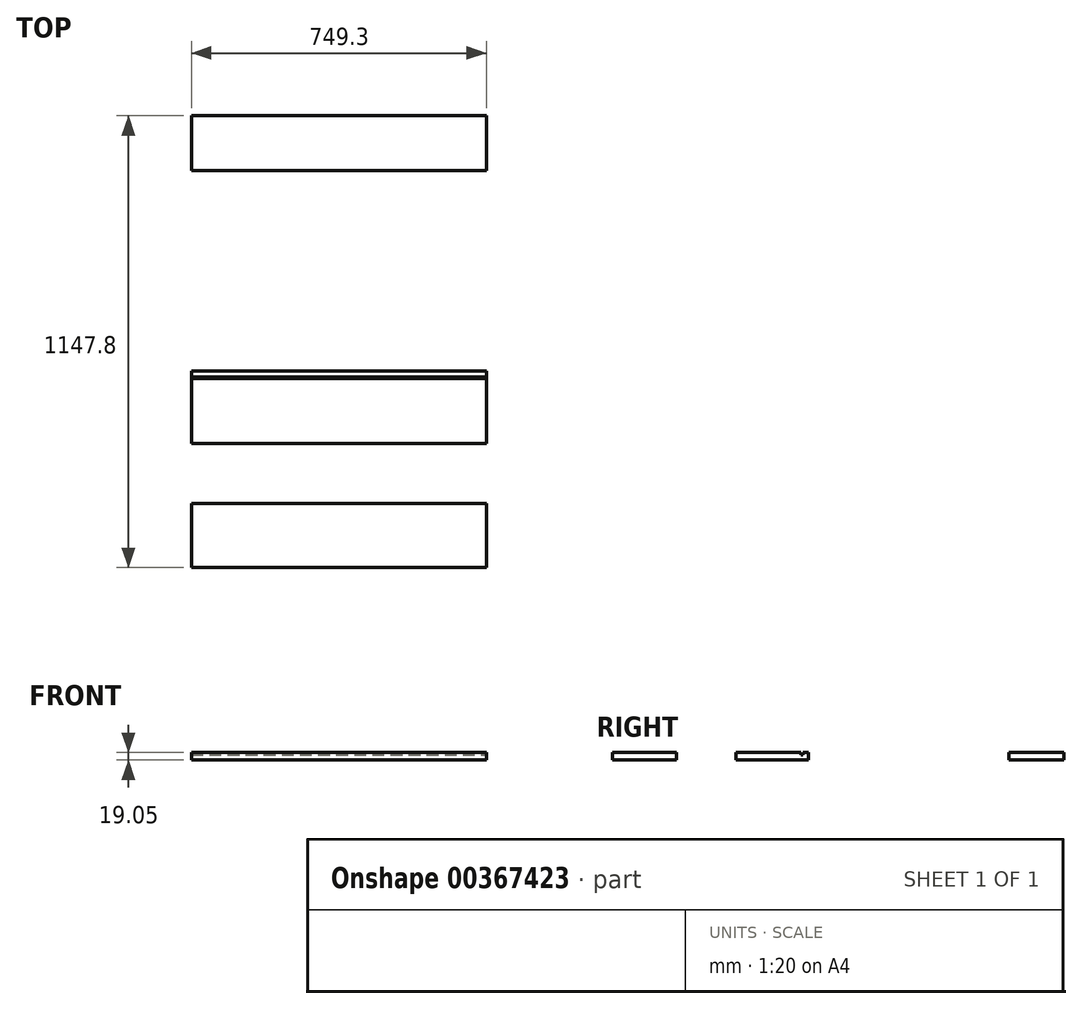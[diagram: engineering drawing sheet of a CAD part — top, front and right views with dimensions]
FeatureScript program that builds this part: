
annotation { "Feature Type Name" : "Feature", "Feature Type Description" : "" }
export const myFeature = defineFeature(function(context is Context, id is Id, definition is map)
    precondition{}
    {
        {
            var Q0;
            Q0=qCreatedBy(makeId("Top.planeOp"),FACE);
            var sketch = newSketch(context, id + "F0", { "sketchPlane" : qUnion([Q0])});
            skLineSegment(sketch, "E0.bottom", {"start": v(374.65, 81.76) * mm, "end": v(-374.65, 81.76) * mm});
            skLineSegment(sketch, "E0.top", {"start": v(374.65, -81.76) * mm, "end": v(-374.65, -81.76) * mm});
            skLineSegment(sketch, "E0.left", {"start": v(374.65, 81.76) * mm, "end": v(374.65, -81.76) * mm});
            skLineSegment(sketch, "E0.right", {"start": v(-374.65, 81.76) * mm, "end": v(-374.65, -81.76) * mm});
            skPoint(sketch, "E0.middle", {"position": v(0, 0) * mm});
            skSolve(sketch);
        }
        {
            var Q0;
            Q0 = qSketchRegion(id + "F0", true);
            extrude(context, id + "F1", {"entities" : qUnion([Q0]), "depth" : 19.05 * mm});
        }
        {
            var Q0;
            Q0=qCreatedBy(makeId("Top.planeOp"),FACE);
            var sketch = newSketch(context, id + "F2", { "sketchPlane" : qUnion([Q0])});
            skLineSegment(sketch, "E1.bottom", {"start": v(374.65, 417.08) * mm, "end": v(-374.65, 417.08) * mm});
            skLineSegment(sketch, "E1.top", {"start": v(374.65, 232.93) * mm, "end": v(-374.65, 232.93) * mm});
            skLineSegment(sketch, "E1.left", {"start": v(374.65, 417.08) * mm, "end": v(374.65, 232.93) * mm});
            skLineSegment(sketch, "E1.right", {"start": v(-374.65, 417.08) * mm, "end": v(-374.65, 232.93) * mm});
            skPoint(sketch, "E1.middle", {"position": v(0, 325) * mm});
            skSolve(sketch);
        }
        {
            var Q0;
            Q0 = qSketchRegion(id + "F2", true);
            extrude(context, id + "F3", {"entities" : qUnion([Q0]), "depth" : 19.05 * mm});
        }
        {
            var Q0;
            Q0=makeQuery(id+"F3.opExtrude","CAP_FACE",FACE,{"disambiguationData":[OSD([sQuery(id+"F2.wireOp",EDGE,"E1.bottom"),sQuery(id+"F2.wireOp",EDGE,"E1.top"),sQuery(id+"F2.wireOp",EDGE,"E1.left"),sQuery(id+"F2.wireOp",EDGE,"E1.right")])],"isStart":false});
            var sketch = newSketch(context, id + "F4", { "sketchPlane" : qUnion([Q0])});
            skLineSegment(sketch, "E2.bottom", {"start": v(-374.65, 402.8) * mm, "end": v(374.65, 402.8) * mm});
            skLineSegment(sketch, "E2.top", {"start": v(-374.65, 398.03) * mm, "end": v(374.65, 398.03) * mm});
            skLineSegment(sketch, "E2.left", {"start": v(-374.65, 402.8) * mm, "end": v(-374.65, 398.03) * mm});
            skLineSegment(sketch, "E2.right", {"start": v(374.65, 402.8) * mm, "end": v(374.65, 398.03) * mm});
            skSolve(sketch);
        }
        {
            var Q0;
            Q0 = qSketchRegion(id + "F4", true);
            extrude(context, id + "F5", {"entities" : qUnion([Q0]), "operationType" : NewBodyOperationType.REMOVE, "oppositeDirection" : true, "depth" : 6.35 * mm});
        }
        {
            var Q0;
            Q0=qCreatedBy(makeId("Top.planeOp"),FACE);
            var sketch = newSketch(context, id + "F6", { "sketchPlane" : qUnion([Q0])});
            skLineSegment(sketch, "E3.bottom", {"start": v(374.65, 1066.04) * mm, "end": v(-374.65, 1066.04) * mm});
            skLineSegment(sketch, "E3.top", {"start": v(374.65, 926.34) * mm, "end": v(-374.65, 926.34) * mm});
            skLineSegment(sketch, "E3.left", {"start": v(374.65, 1066.04) * mm, "end": v(374.65, 926.34) * mm});
            skLineSegment(sketch, "E3.right", {"start": v(-374.65, 1066.04) * mm, "end": v(-374.65, 926.34) * mm});
            skPoint(sketch, "E3.middle", {"position": v(0, 996.19) * mm});
            skSolve(sketch);
        }
        {
            var Q0;
            Q0 = qSketchRegion(id + "F6", true);
            extrude(context, id + "F7", {"entities" : qUnion([Q0]), "depth" : 19.05 * mm});
        }
    });
